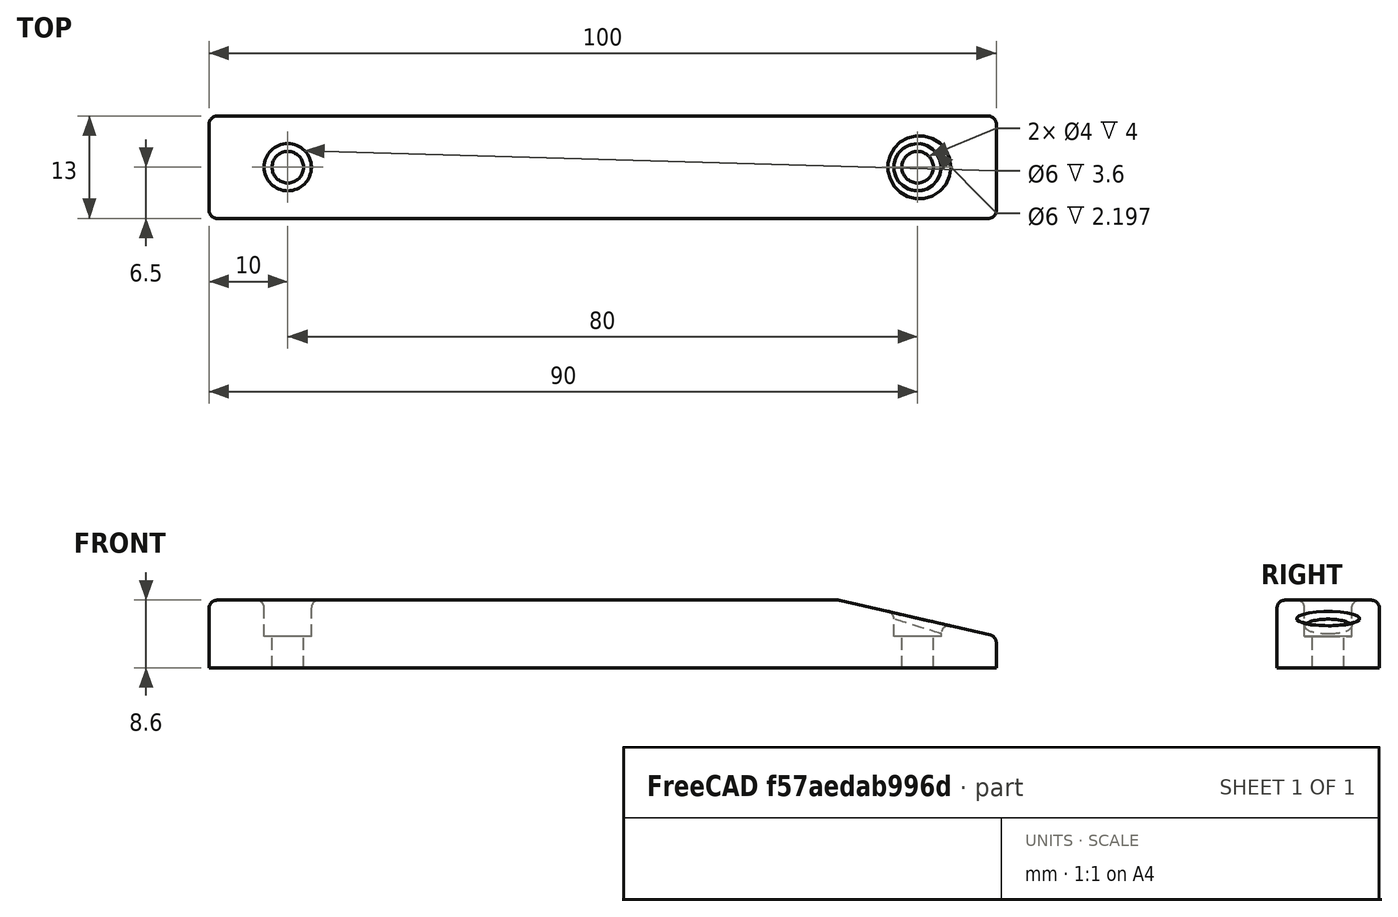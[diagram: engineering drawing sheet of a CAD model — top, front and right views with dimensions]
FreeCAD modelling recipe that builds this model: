
FCSTD DOCUMENT  (FreeCAD 0.14R3700 (Git))
Label: Igus-Distance-Base
License: CC-BY 3.0
LicenseURL: http://creativecommons.org/licenses/by/3.0/
objects: Part::Cylinder×4, Part::Cut×3, Part::MultiFuse×2, Part::Box×1, Part::Wedge×1, Part::Fillet×1
note: 12 computed .brp shape members not serialized (recipe doc carries the construction recipe); baked Part::Feature solids carry a one-line shape summary decoded from their .brp

FEATURE [Part::Box] Box  label="Cube"
  Height = 8.6
  Length = 100
  Width = 13
FEATURE [Part::Cylinder] Cylinder  label="M3-Head"
  Angle = 360
  Height = 10
  Placement = pos=(0,0,4) rot=(0,0,1;0rad)
  Radius = 3
FEATURE [Part::Cylinder] Cylinder001  label="M3-Whole"
  Angle = 360
  Height = 10
  Radius = 2
FEATURE [Part::MultiFuse] Fusion  label="M3-Fusion"
  Placement = pos=(10,6.5,0) rot=(0,0,1;0rad)
  Shapes = -> [Cylinder001,Cylinder]
FEATURE [Part::Cylinder] Cylinder002  label="M3-Head001"
  Angle = 360
  Height = 10
  Placement = pos=(0,0,4) rot=(0,0,1;0rad)
  Radius = 3
FEATURE [Part::Cylinder] Cylinder003  label="M3-Whole001"
  Angle = 360
  Height = 10
  Radius = 2
FEATURE [Part::MultiFuse] Fusion001  label="M3-Fusion-2"
  Placement = pos=(90,6.5,0) rot=(0,0,1;0rad)
  Shapes = -> [Cylinder003,Cylinder002]
FEATURE [Part::Cut] Cut
  Base = -> Box
  Tool = -> Fusion
FEATURE [Part::Cut] Cut001
  Base = -> Cut
  Tool = -> Fusion001
FEATURE [Part::Wedge] Wedge001  label="Wedge"
  Placement = pos=(100,0,0) rot=(0,0,1;1.5708rad)
  X2max = 13
  X2min = 0
  Xmax = 13
  Xmin = 0
  Ymax = 20
  Ymin = 0
  Z2max = 8.6
  Z2min = 8.6
  Zmax = 8.6
  Zmin = 4
FEATURE [Part::Cut] Cut002
  Base = -> Cut001
  Tool = -> Wedge001
FEATURE [Part::Fillet] Fillet  label="Igus-Distance-Base"
  Base = -> Cut002
  Edges = 13 edges r=1: [Edge1,Edge2,Edge3,Edge5,Edge6,Edge7,Edge9,Edge10,Edge11,Edge12,Edge13,Edge18,Edge19]
